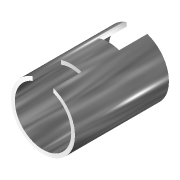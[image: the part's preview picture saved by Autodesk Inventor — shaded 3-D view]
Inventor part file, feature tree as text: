
AUTODESK INVENTOR PART (.ipt)
format: ipt  version: 2020.3 (Build 243373010, 373A)  size: 113,664 bytes
history: native  units: mm
features: extrude x2, sketch x2, mirror x1, projected_geometry x1
ambient origin geometry x8: Origin, YZ Plane, XZ Plane, XY Plane, X Axis, Y Axis, Z Axis, Center Point
bodies: Solid1 (feature_tree)
feature tree (6):
  extrude  "Extrusion1"  Depth=17.0mm
  extrude  "Extrusion2"  Depth=7.5mm TaperAngle=0.0deg
  mirror  "Mirror1"
  sketch  "Sketch1"  dims[d0=15.0mm d1=17.0mm]
  sketch  "Sketch2"  dims[d2=25.0mm d3=0.0mm d4=7.5mm d5=0.0mm]
  projected_geometry  "Projected Loop1"
